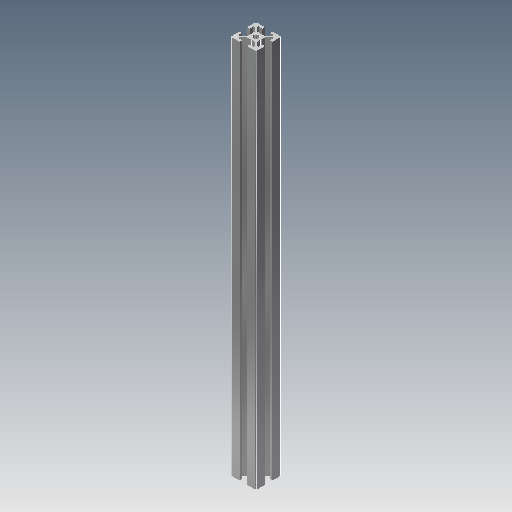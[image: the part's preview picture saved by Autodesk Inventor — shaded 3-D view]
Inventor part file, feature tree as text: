
AUTODESK INVENTOR PART (.ipt)
format: ipt  version: 2018.2 (Build 222227000, 227)  size: 162,304 bytes
history: native  units: mm
features: extrude x1, sketch x1
ambient origin geometry x8: Origin, YZ Plane, XZ Plane, XY Plane, X Axis, Y Axis, Z Axis, Center Point
bodies: Solid1 (feature_tree)
feature tree (2):
  extrude  "Extrusion1"  [1 undecoded]
  sketch  "Sketch1"  dims[d0=300.0mm d1=0.0mm]
note: 1 required parameter value undecoded (feature->parameter linkage not recoverable at this tier; creation-order binding heuristic only, values carry confidence <= 0.55)
